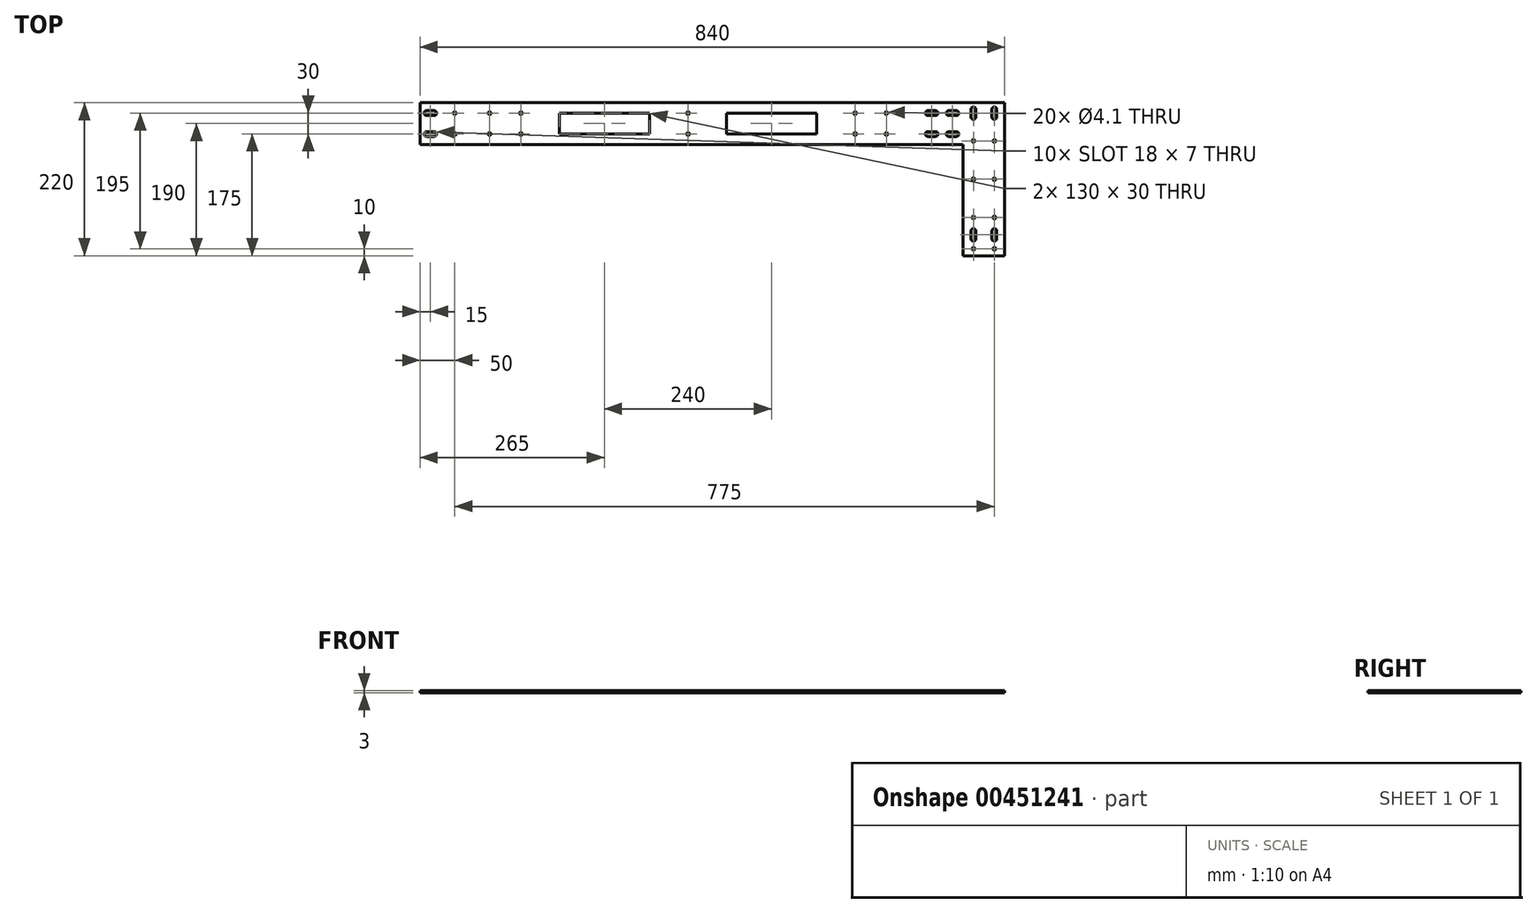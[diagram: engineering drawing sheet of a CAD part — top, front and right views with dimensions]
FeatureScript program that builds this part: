
annotation { "Feature Type Name" : "Feature", "Feature Type Description" : "" }
export const myFeature = defineFeature(function(context is Context, id is Id, definition is map)
    precondition{}
    {
        {
            var Q0;
            Q0=qCreatedBy(makeId("Top.planeOp"),FACE);
            var sketch = newSketch(context, id + "F0", { "sketchPlane" : qUnion([Q0])});
            skLineSegment(sketch, "E0.bottom", {"start": v(60, -30) * mm, "end": v(-60, -30) * mm});
            skLineSegment(sketch, "E0.top", {"start": v(60, 30) * mm, "end": v(-60, 30) * mm});
            skLineSegment(sketch, "E0.left", {"start": v(60, -30) * mm, "end": v(60, 30) * mm});
            skLineSegment(sketch, "E0.right", {"start": v(-60, -30) * mm, "end": v(-60, 30) * mm});
            skPoint(sketch, "E0.middle", {"position": v(0, 0) * mm});
            skLineSegment(sketch, "E1", {"start": v(60, -30) * mm, "end": v(60, -190) * mm});
            skLineSegment(sketch, "E2", {"start": v(60, -190) * mm, "end": v(0, -190) * mm});
            skLineSegment(sketch, "E3", {"start": v(0, -190) * mm, "end": v(0, -30) * mm});
            skSolve(sketch);
        }
        {
            var Q0;
            Q0=qSketchRegion(id+"F0",true);
            extrude(context, id + "F1", {"entities" : qUnion([Q0]), "depth" : 3 * mm, "offsetDistance" : 25 * mm});
        }
        {
            var Q0;
            Q0=makeQuery(id+"F1.opExtrude","CAP_FACE",FACE,{"disambiguationData":[OSD([sQuery(id+"F0.wireOp",EDGE,"E0.bottom"),sQuery(id+"F0.wireOp",EDGE,"E0.top"),sQuery(id+"F0.wireOp",EDGE,"E0.left"),sQuery(id+"F0.wireOp",EDGE,"E0.right"),sQuery(id+"F0.wireOp",EDGE,"E1"),sQuery(id+"F0.wireOp",EDGE,"E2"),sQuery(id+"F0.wireOp",EDGE,"E3")])],"isStart":false});
            var sketch = newSketch(context, id + "F2", { "sketchPlane" : qUnion([Q0])});
            skLineSegment(sketch, "E4.bottom", {"start": v(-39.5, 11.5) * mm, "end": v(-50.5, 11.5) * mm});
            skLineSegment(sketch, "E4.top", {"start": v(-39.5, 18.5) * mm, "end": v(-50.5, 18.5) * mm});
            skLineSegment(sketch, "E4.left", {"start": v(-39.5, 11.5) * mm, "end": v(-39.5, 18.5) * mm, "construction": true});
            skLineSegment(sketch, "E4.right", {"start": v(-50.5, 11.5) * mm, "end": v(-50.5, 18.5) * mm, "construction": true});
            skPoint(sketch, "E4.middle", {"position": v(-45, 15) * mm});
            skArc(sketch, "E5", {"start": v(-39.5, 11.5) * mm, "mid": v(-36, 15) * mm, "end": v(-39.5, 18.5) * mm});
            skArc(sketch, "E6", {"start": v(-50.5, 18.5) * mm, "mid": v(-54, 15) * mm, "end": v(-50.5, 11.5) * mm});
            skLineSegment(sketch, "E7.bottom", {"start": v(-20.5, 11.5) * mm, "end": v(-9.5, 11.5) * mm});
            skLineSegment(sketch, "E7.top", {"start": v(-20.5, 18.5) * mm, "end": v(-9.5, 18.5) * mm});
            skLineSegment(sketch, "E7.left", {"start": v(-20.5, 11.5) * mm, "end": v(-20.5, 18.5) * mm, "construction": true});
            skLineSegment(sketch, "E7.right", {"start": v(-9.5, 11.5) * mm, "end": v(-9.5, 18.5) * mm, "construction": true});
            skPoint(sketch, "E7.middle", {"position": v(-15, 15) * mm});
            skArc(sketch, "E8", {"start": v(-20.5, 18.5) * mm, "mid": v(-24, 15) * mm, "end": v(-20.5, 11.5) * mm});
            skArc(sketch, "E9", {"start": v(-9.5, 11.5) * mm, "mid": v(-6, 15) * mm, "end": v(-9.5, 18.5) * mm});
            skLineSegment(sketch, "E10.MirrorCS", {"start": v(-39.5, -11.5) * mm, "end": v(-39.5, -18.5) * mm, "construction": true});
            skLineSegment(sketch, "E11.MirrorCS", {"start": v(-50.5, -11.5) * mm, "end": v(-50.5, -18.5) * mm, "construction": true});
            skLineSegment(sketch, "E12.MirrorCS", {"start": v(-20.5, -11.5) * mm, "end": v(-20.5, -18.5) * mm, "construction": true});
            skLineSegment(sketch, "E13.MirrorCS", {"start": v(-9.5, -11.5) * mm, "end": v(-9.5, -18.5) * mm, "construction": true});
            skArc(sketch, "E14.MirrorCS", {"start": v(-50.5, -18.5) * mm, "mid": v(-54, -15) * mm, "end": v(-50.5, -11.5) * mm});
            skPoint(sketch, "E15.MirrorP", {"position": v(-45, -15) * mm});
            skLineSegment(sketch, "E16.MirrorCS", {"start": v(-20.5, -18.5) * mm, "end": v(-9.5, -18.5) * mm});
            skArc(sketch, "E17.MirrorCS", {"start": v(-39.5, -11.5) * mm, "mid": v(-36, -15) * mm, "end": v(-39.5, -18.5) * mm});
            skLineSegment(sketch, "E18.MirrorCS", {"start": v(-20.5, -11.5) * mm, "end": v(-9.5, -11.5) * mm});
            skPoint(sketch, "E19.MirrorP", {"position": v(-15, -15) * mm});
            skArc(sketch, "E20.MirrorCS", {"start": v(-20.5, -18.5) * mm, "mid": v(-24, -15) * mm, "end": v(-20.5, -11.5) * mm});
            skArc(sketch, "E21.MirrorCS", {"start": v(-9.5, -11.5) * mm, "mid": v(-6, -15) * mm, "end": v(-9.5, -18.5) * mm});
            skLineSegment(sketch, "E22.MirrorCS", {"start": v(-39.5, -18.5) * mm, "end": v(-50.5, -18.5) * mm});
            skLineSegment(sketch, "E23.MirrorCS", {"start": v(-39.5, -11.5) * mm, "end": v(-50.5, -11.5) * mm});
            skLineSegment(sketch, "E24.bottom", {"start": v(48.5, -165.5) * mm, "end": v(41.5, -165.5) * mm, "construction": true});
            skLineSegment(sketch, "E24.top", {"start": v(48.5, -154.5) * mm, "end": v(41.5, -154.5) * mm, "construction": true});
            skLineSegment(sketch, "E24.left", {"start": v(48.5, -165.5) * mm, "end": v(48.5, -154.5) * mm});
            skLineSegment(sketch, "E24.right", {"start": v(41.5, -165.5) * mm, "end": v(41.5, -154.5) * mm});
            skPoint(sketch, "E24.middle", {"position": v(45, -160) * mm});
            skArc(sketch, "E25", {"start": v(48.5, -154.5) * mm, "mid": v(45, -151) * mm, "end": v(41.5, -154.5) * mm});
            skArc(sketch, "E26", {"start": v(41.5, -165.5) * mm, "mid": v(45, -169) * mm, "end": v(48.5, -165.5) * mm});
            skLineSegment(sketch, "E27.bottom", {"start": v(18.5, -165.5) * mm, "end": v(11.5, -165.5) * mm, "construction": true});
            skLineSegment(sketch, "E27.top", {"start": v(18.5, -154.5) * mm, "end": v(11.5, -154.5) * mm, "construction": true});
            skLineSegment(sketch, "E27.left", {"start": v(18.5, -165.5) * mm, "end": v(18.5, -154.5) * mm});
            skLineSegment(sketch, "E27.right", {"start": v(11.5, -165.5) * mm, "end": v(11.5, -154.5) * mm});
            skPoint(sketch, "E27.middle", {"position": v(15, -160) * mm});
            skArc(sketch, "E28", {"start": v(18.5, -154.5) * mm, "mid": v(15, -151) * mm, "end": v(11.5, -154.5) * mm});
            skArc(sketch, "E29", {"start": v(11.5, -165.5) * mm, "mid": v(15, -169) * mm, "end": v(18.5, -165.5) * mm});
            skCircle(sketch, "E30", {"center": v(15, -180) * mm, "radius": 2.05 * mm});
            skCircle(sketch, "E31", {"center": v(45, -180) * mm, "radius": 2.05 * mm});
            skCircle(sketch, "E32", {"center": v(15, -135) * mm, "radius": 2.05 * mm});
            skCircle(sketch, "E33", {"center": v(45, -135) * mm, "radius": 2.05 * mm});
            skPoint(sketch, "E34.middle.positionSnap0", {"position": v(30, -190) * mm});
            skPoint(sketch, "E34.centerSnap0", {"position": v(30, -190) * mm});
            skLineSegment(sketch, "E35.bottom", {"start": v(48.5, 9.5) * mm, "end": v(41.5, 9.5) * mm, "construction": true});
            skLineSegment(sketch, "E35.top", {"start": v(48.5, 20.5) * mm, "end": v(41.5, 20.5) * mm, "construction": true});
            skLineSegment(sketch, "E35.left", {"start": v(48.5, 9.5) * mm, "end": v(48.5, 20.5) * mm});
            skLineSegment(sketch, "E35.right", {"start": v(41.5, 9.5) * mm, "end": v(41.5, 20.5) * mm});
            skPoint(sketch, "E35.middle", {"position": v(45, 15) * mm});
            skArc(sketch, "E36", {"start": v(48.5, 20.5) * mm, "mid": v(45, 24) * mm, "end": v(41.5, 20.5) * mm});
            skArc(sketch, "E37", {"start": v(41.5, 9.5) * mm, "mid": v(45, 6) * mm, "end": v(48.5, 9.5) * mm});
            skLineSegment(sketch, "E38.bottom", {"start": v(18.5, 9.5) * mm, "end": v(11.5, 9.5) * mm, "construction": true});
            skLineSegment(sketch, "E38.top", {"start": v(18.5, 20.5) * mm, "end": v(11.5, 20.5) * mm, "construction": true});
            skLineSegment(sketch, "E38.left", {"start": v(18.5, 9.5) * mm, "end": v(18.5, 20.5) * mm});
            skLineSegment(sketch, "E38.right", {"start": v(11.5, 9.5) * mm, "end": v(11.5, 20.5) * mm});
            skPoint(sketch, "E38.middle", {"position": v(15, 15) * mm});
            skArc(sketch, "E39", {"start": v(18.5, 20.5) * mm, "mid": v(15, 24) * mm, "end": v(11.5, 20.5) * mm});
            skArc(sketch, "E40", {"start": v(11.5, 9.5) * mm, "mid": v(15, 6) * mm, "end": v(18.5, 9.5) * mm});
            skCircle(sketch, "E41", {"center": v(15, -25) * mm, "radius": 2.05 * mm});
            skCircle(sketch, "E42", {"center": v(45, -25) * mm, "radius": 2.05 * mm});
            skCircle(sketch, "E43", {"center": v(45, -80) * mm, "radius": 2.05 * mm});
            skCircle(sketch, "E44", {"center": v(15, -80) * mm, "radius": 2.05 * mm});
            skSolve(sketch);
        }
        {
            var Q0;
            Q0 = qSketchRegion(id + "F2", true);
            extrude(context, id + "F3", {"entities" : qUnion([Q0]), "operationType" : NewBodyOperationType.REMOVE, "oppositeDirection" : true, "depth" : 3 * mm, "offsetDistance" : 25 * mm});
        }
        {
            var Q0;
            Q0=makeQuery(id+"F1.opExtrude","CAP_FACE",FACE,{"disambiguationData":[OSD([sQuery(id+"F0.wireOp",EDGE,"E0.bottom"),sQuery(id+"F0.wireOp",EDGE,"E0.top"),sQuery(id+"F0.wireOp",EDGE,"E0.left"),sQuery(id+"F0.wireOp",EDGE,"E0.right"),sQuery(id+"F0.wireOp",EDGE,"E1"),sQuery(id+"F0.wireOp",EDGE,"E2"),sQuery(id+"F0.wireOp",EDGE,"E3")])],"isStart":true});
            var sketch = newSketch(context, id + "F4", { "sketchPlane" : qUnion([Q0])});
            skLineSegment(sketch, "E45.bottom", {"start": v(-60, -30) * mm, "end": v(-780, -30) * mm});
            skLineSegment(sketch, "E45.top", {"start": v(-60, 30) * mm, "end": v(-780, 30) * mm});
            skLineSegment(sketch, "E45.left", {"start": v(-60, -30) * mm, "end": v(-60, 30) * mm});
            skLineSegment(sketch, "E45.right", {"start": v(-780, -30) * mm, "end": v(-780, 30) * mm});
            skLineSegment(sketch, "E46.bottom", {"start": v(-759.5, -18.5) * mm, "end": v(-770.5, -18.5) * mm});
            skLineSegment(sketch, "E46.top", {"start": v(-759.5, -11.5) * mm, "end": v(-770.5, -11.5) * mm});
            skLineSegment(sketch, "E46.left", {"start": v(-759.5, -18.5) * mm, "end": v(-759.5, -11.5) * mm, "construction": true});
            skLineSegment(sketch, "E46.right", {"start": v(-770.5, -18.5) * mm, "end": v(-770.5, -11.5) * mm, "construction": true});
            skPoint(sketch, "E46.middle", {"position": v(-765, -15) * mm});
            skArc(sketch, "E47", {"start": v(-759.5, -18.5) * mm, "mid": v(-756, -15) * mm, "end": v(-759.5, -11.5) * mm});
            skArc(sketch, "E48", {"start": v(-770.5, -11.5) * mm, "mid": v(-774, -15) * mm, "end": v(-770.5, -18.5) * mm});
            skLineSegment(sketch, "E49", {"start": v(-772.56, 0) * mm, "end": v(-762.3, 0) * mm, "construction": true});
            skLineSegment(sketch, "E50.MirrorCS", {"start": v(-759.5, 11.5) * mm, "end": v(-770.5, 11.5) * mm});
            skArc(sketch, "E51.MirrorCS", {"start": v(-770.5, 11.5) * mm, "mid": v(-774, 15) * mm, "end": v(-770.5, 18.5) * mm});
            skPoint(sketch, "E52.MirrorP", {"position": v(-765, 15) * mm});
            skArc(sketch, "E53.MirrorCS", {"start": v(-759.5, 18.5) * mm, "mid": v(-756, 15) * mm, "end": v(-759.5, 11.5) * mm});
            skLineSegment(sketch, "E54.MirrorCS", {"start": v(-759.5, 18.5) * mm, "end": v(-759.5, 11.5) * mm, "construction": true});
            skLineSegment(sketch, "E55.MirrorCS", {"start": v(-770.5, 18.5) * mm, "end": v(-770.5, 11.5) * mm, "construction": true});
            skLineSegment(sketch, "E56.MirrorCS", {"start": v(-759.5, 18.5) * mm, "end": v(-770.5, 18.5) * mm});
            skCircle(sketch, "E57", {"center": v(-680, -15) * mm, "radius": 2.05 * mm});
            skCircle(sketch, "E58", {"center": v(-680, 15) * mm, "radius": 2.05 * mm});
            skCircle(sketch, "E59", {"center": v(-110, -15) * mm, "radius": 2.05 * mm});
            skCircle(sketch, "E60", {"center": v(-110, 15) * mm, "radius": 2.05 * mm});
            skCircle(sketch, "E61", {"center": v(-730, -15) * mm, "radius": 2.05 * mm});
            skCircle(sketch, "E62", {"center": v(-730, 15) * mm, "radius": 2.05 * mm});
            skCircle(sketch, "E63", {"center": v(-155, 15) * mm, "radius": 2.05 * mm});
            skPoint(sketch, "E63.centerSnap0", {"position": v(-60, 0) * mm});
            skCircle(sketch, "E64", {"center": v(-395, 15) * mm, "radius": 2.05 * mm});
            skCircle(sketch, "E65", {"center": v(-635, 15) * mm, "radius": 2.05 * mm});
            skCircle(sketch, "E66", {"center": v(-635, -15) * mm, "radius": 2.05 * mm});
            skCircle(sketch, "E67", {"center": v(-395, -15) * mm, "radius": 2.05 * mm});
            skCircle(sketch, "E68", {"center": v(-155, -15) * mm, "radius": 2.05 * mm});
            skSolve(sketch);
        }
        {
            var Q0;
            Q0 = qSketchRegion(id + "F4", true);
            extrude(context, id + "F5", {"entities" : qUnion([Q0]), "operationType" : NewBodyOperationType.ADD, "oppositeDirection" : true, "depth" : 3 * mm, "offsetDistance" : 25 * mm});
        }
        {
            var Q0;
            Q0=makeQuery(id+"F5.boolean.opBoolean","MERGE",FACE,{"derivedFrom":[makeQuery(id+"F1.opExtrude","CAP_FACE",FACE,{"disambiguationData":[OSD([sQuery(id+"F0.wireOp",EDGE,"E0.bottom"),sQuery(id+"F0.wireOp",EDGE,"E0.top"),sQuery(id+"F0.wireOp",EDGE,"E0.left"),sQuery(id+"F0.wireOp",EDGE,"E0.right"),sQuery(id+"F0.wireOp",EDGE,"E1"),sQuery(id+"F0.wireOp",EDGE,"E2"),sQuery(id+"F0.wireOp",EDGE,"E3")])],"isStart":true}),makeQuery(id+"F5.opExtrude","CAP_FACE",FACE,{"disambiguationData":[OSD([sQuery(id+"F4.wireOp",EDGE,"E45.bottom"),sQuery(id+"F4.wireOp",EDGE,"E45.top"),sQuery(id+"F4.wireOp",EDGE,"E45.left"),sQuery(id+"F4.wireOp",EDGE,"E45.right"),sQuery(id+"F4.wireOp",EDGE,"E46.bottom"),sQuery(id+"F4.wireOp",EDGE,"E46.top"),sQuery(id+"F4.wireOp",EDGE,"E47"),sQuery(id+"F4.wireOp",EDGE,"E48"),sQuery(id+"F4.wireOp",EDGE,"E50.MirrorCS"),sQuery(id+"F4.wireOp",EDGE,"E51.MirrorCS"),sQuery(id+"F4.wireOp",EDGE,"E53.MirrorCS"),sQuery(id+"F4.wireOp",EDGE,"E56.MirrorCS"),sQuery(id+"F4.wireOp",EDGE,"E57"),sQuery(id+"F4.wireOp",EDGE,"E58"),sQuery(id+"F4.wireOp",EDGE,"E59"),sQuery(id+"F4.wireOp",EDGE,"E60"),sQuery(id+"F4.wireOp",EDGE,"E61"),sQuery(id+"F4.wireOp",EDGE,"E62"),sQuery(id+"F4.wireOp",EDGE,"E63"),sQuery(id+"F4.wireOp",EDGE,"E64"),sQuery(id+"F4.wireOp",EDGE,"E65")])],"isStart":true})]});
            var sketch = newSketch(context, id + "F6", { "sketchPlane" : qUnion([Q0])});
            skLineSegment(sketch, "E69.bottom", {"start": v(-450, -15) * mm, "end": v(-580, -15) * mm});
            skLineSegment(sketch, "E69.top", {"start": v(-450, 15) * mm, "end": v(-580, 15) * mm});
            skLineSegment(sketch, "E69.left", {"start": v(-450, -15) * mm, "end": v(-450, 15) * mm});
            skLineSegment(sketch, "E69.right", {"start": v(-580, -15) * mm, "end": v(-580, 15) * mm});
            skPoint(sketch, "E69.middle", {"position": v(-515, 0) * mm});
            skLineSegment(sketch, "E70.bottom", {"start": v(-210, -15) * mm, "end": v(-340, -15) * mm});
            skLineSegment(sketch, "E70.top", {"start": v(-210, 15) * mm, "end": v(-340, 15) * mm});
            skLineSegment(sketch, "E70.left", {"start": v(-210, -15) * mm, "end": v(-210, 15) * mm});
            skLineSegment(sketch, "E70.right", {"start": v(-340, -15) * mm, "end": v(-340, 15) * mm});
            skPoint(sketch, "E70.middle", {"position": v(-275, 0) * mm});
            skPoint(sketch, "E71", {"position": v(-155, 15) * mm});
            skPoint(sketch, "E72", {"position": v(-395, 15) * mm});
            skSolve(sketch);
        }
        {
            var Q0;
            Q0 = qSketchRegion(id + "F6", true);
            extrude(context, id + "F7", {"entities" : qUnion([Q0]), "operationType" : NewBodyOperationType.REMOVE, "oppositeDirection" : true, "depth" : 25 * mm, "offsetDistance" : 25 * mm});
        }
    });
